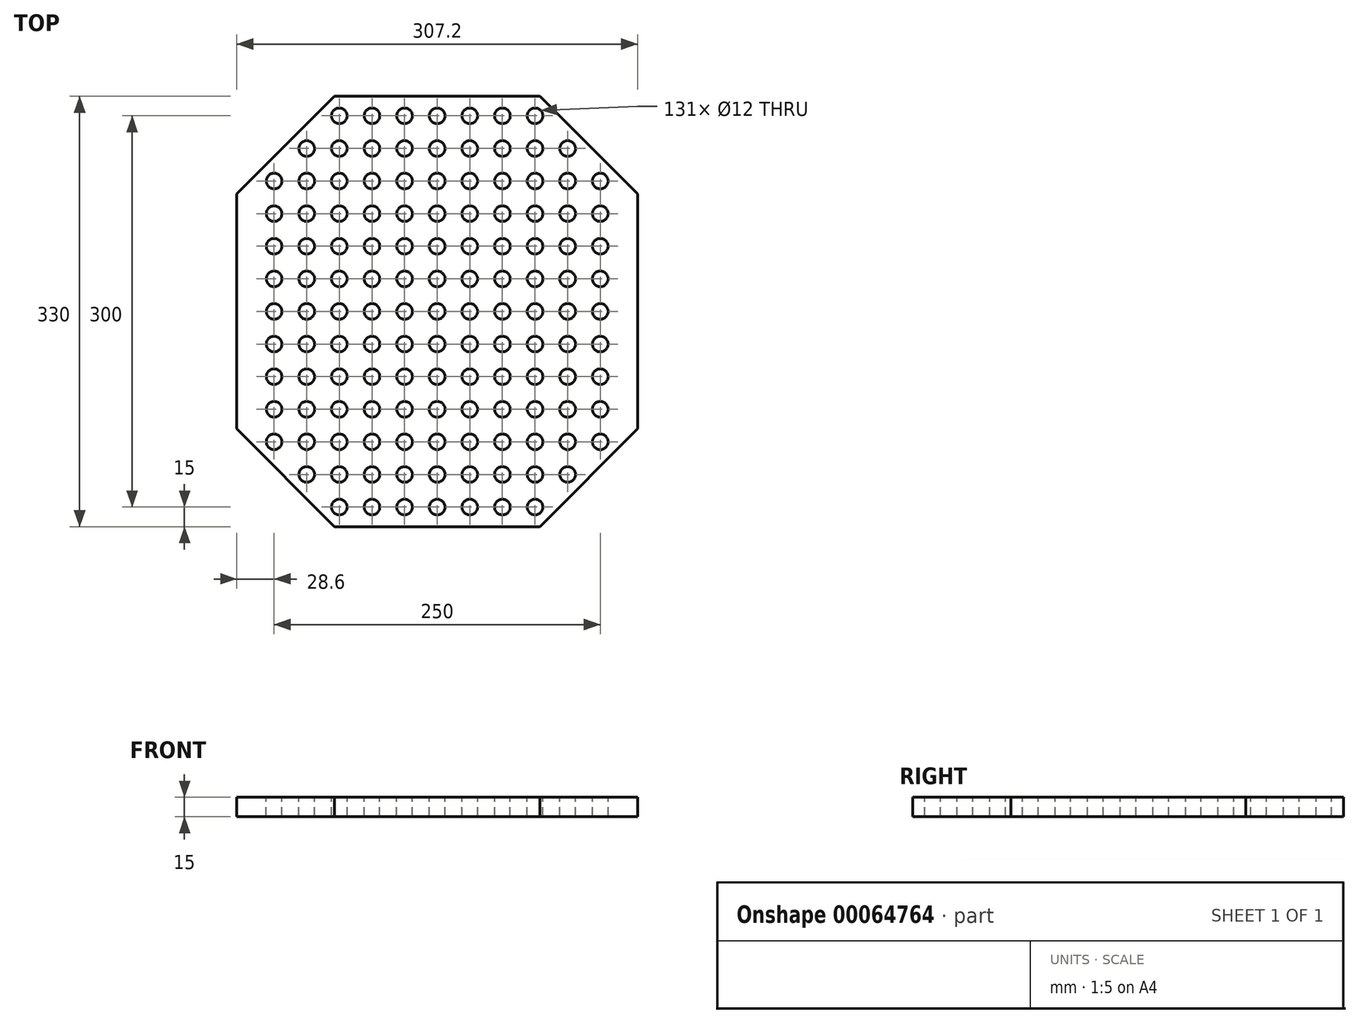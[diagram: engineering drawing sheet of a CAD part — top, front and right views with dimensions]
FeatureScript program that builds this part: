
annotation { "Feature Type Name" : "Feature", "Feature Type Description" : "" }
export const myFeature = defineFeature(function(context is Context, id is Id, definition is map)
    precondition{}
    {
        {
            var Q0;
            Q0=qCreatedBy(makeId("Top.planeOp"),FACE);
            var sketch = newSketch(context, id + "F0", { "sketchPlane" : qUnion([Q0])});
            skCircle(sketch, "E0", {"center": v(0, 0) * mm, "radius": 228.6 * mm, "construction": true});
            skLineSegment(sketch, "E1", {"start": v(0, 165) * mm, "end": v(78.6, 165) * mm});
            skLineSegment(sketch, "E2", {"start": v(78.6, 165) * mm, "end": v(153.6, 90) * mm});
            skLineSegment(sketch, "E3", {"start": v(153.6, 90) * mm, "end": v(153.6, 0) * mm});
            skLineSegment(sketch, "E4", {"start": v(0, 0) * mm, "end": v(0, 165) * mm, "construction": true});
            skLineSegment(sketch, "E5", {"start": v(0, 0) * mm, "end": v(153.6, 0) * mm, "construction": true});
            skLineSegment(sketch, "E6", {"start": v(0, 165) * mm, "end": v(0, 0) * mm});
            skLineSegment(sketch, "E7", {"start": v(0, 0) * mm, "end": v(153.6, 0) * mm});
            skSolve(sketch);
        }
        {
            var Q0;
            Q0 = qSketchRegion(id + "F0", true);
            extrude(context, id + "F1", {"entities" : qUnion([Q0]), "oppositeDirection" : true, "depth" : 15 * mm});
        }
        {
            var Q0;
            Q0=qCreatedBy(makeId("Top.planeOp"),FACE);
            var sketch = newSketch(context, id + "F2", { "sketchPlane" : qUnion([Q0])});
            skCircle(sketch, "E8", {"center": v(0, 0) * mm, "radius": 6 * mm});
            skCircle(sketch, "E9.0.1.0", {"center": v(0, 25) * mm, "radius": 6 * mm});
            skCircle(sketch, "E9.0.2.0", {"center": v(0, 50) * mm, "radius": 6 * mm});
            skCircle(sketch, "E9.0.3.0", {"center": v(0, 75) * mm, "radius": 6 * mm});
            skCircle(sketch, "E9.0.4.0", {"center": v(0, 100) * mm, "radius": 6 * mm});
            skCircle(sketch, "E9.0.5.0", {"center": v(0, 125) * mm, "radius": 6 * mm});
            skCircle(sketch, "E9.0.6.0", {"center": v(0, 150) * mm, "radius": 6 * mm});
            skCircle(sketch, "E9.1.0.0", {"center": v(25, 0) * mm, "radius": 6 * mm});
            skCircle(sketch, "E9.1.1.0", {"center": v(25, 25) * mm, "radius": 6 * mm});
            skCircle(sketch, "E9.1.2.0", {"center": v(25, 50) * mm, "radius": 6 * mm});
            skCircle(sketch, "E9.1.3.0", {"center": v(25, 75) * mm, "radius": 6 * mm});
            skCircle(sketch, "E9.1.4.0", {"center": v(25, 100) * mm, "radius": 6 * mm});
            skCircle(sketch, "E9.1.5.0", {"center": v(25, 125) * mm, "radius": 6 * mm});
            skCircle(sketch, "E9.1.6.0", {"center": v(25, 150) * mm, "radius": 6 * mm});
            skCircle(sketch, "E9.2.0.0", {"center": v(50, 0) * mm, "radius": 6 * mm});
            skCircle(sketch, "E9.2.1.0", {"center": v(50, 25) * mm, "radius": 6 * mm});
            skCircle(sketch, "E9.2.2.0", {"center": v(50, 50) * mm, "radius": 6 * mm});
            skCircle(sketch, "E9.2.3.0", {"center": v(50, 75) * mm, "radius": 6 * mm});
            skCircle(sketch, "E9.2.4.0", {"center": v(50, 100) * mm, "radius": 6 * mm});
            skCircle(sketch, "E9.2.5.0", {"center": v(50, 125) * mm, "radius": 6 * mm});
            skCircle(sketch, "E9.2.6.0", {"center": v(50, 150) * mm, "radius": 6 * mm});
            skCircle(sketch, "E9.3.0.0", {"center": v(75, 0) * mm, "radius": 6 * mm});
            skCircle(sketch, "E9.3.1.0", {"center": v(75, 25) * mm, "radius": 6 * mm});
            skCircle(sketch, "E9.3.2.0", {"center": v(75, 50) * mm, "radius": 6 * mm});
            skCircle(sketch, "E9.3.3.0", {"center": v(75, 75) * mm, "radius": 6 * mm});
            skCircle(sketch, "E9.3.4.0", {"center": v(75, 100) * mm, "radius": 6 * mm});
            skCircle(sketch, "E9.3.5.0", {"center": v(75, 125) * mm, "radius": 6 * mm});
            skCircle(sketch, "E9.3.6.0", {"center": v(75, 150) * mm, "radius": 6 * mm});
            skCircle(sketch, "E9.4.0.0", {"center": v(100, 0) * mm, "radius": 6 * mm});
            skCircle(sketch, "E9.4.1.0", {"center": v(100, 25) * mm, "radius": 6 * mm});
            skCircle(sketch, "E9.4.2.0", {"center": v(100, 50) * mm, "radius": 6 * mm});
            skCircle(sketch, "E9.4.3.0", {"center": v(100, 75) * mm, "radius": 6 * mm});
            skCircle(sketch, "E9.4.4.0", {"center": v(100, 100) * mm, "radius": 6 * mm});
            skCircle(sketch, "E9.4.5.0", {"center": v(100, 125) * mm, "radius": 6 * mm});
            skCircle(sketch, "E9.5.0.0", {"center": v(125, 0) * mm, "radius": 6 * mm});
            skCircle(sketch, "E9.5.1.0", {"center": v(125, 25) * mm, "radius": 6 * mm});
            skCircle(sketch, "E9.5.2.0", {"center": v(125, 50) * mm, "radius": 6 * mm});
            skCircle(sketch, "E9.5.3.0", {"center": v(125, 75) * mm, "radius": 6 * mm});
            skCircle(sketch, "E9.5.4.0", {"center": v(125, 100) * mm, "radius": 6 * mm});
            skLineSegment(sketch, "E9.direction1", {"start": v(0, 0) * mm, "end": v(25, 0) * mm, "construction": true});
            skLineSegment(sketch, "E9.direction2", {"start": v(0, 0) * mm, "end": v(0, 25) * mm, "construction": true});
            skSolve(sketch);
        }
        {
            var Q0;
            Q0 = qSketchRegion(id + "F2", true);
            extrude(context, id + "F3", {"entities" : qUnion([Q0]), "operationType" : NewBodyOperationType.REMOVE, "oppositeDirection" : true, "depth" : 25 * mm});
        }
        {
            var Q0;
            Q0=makeQuery(id+"F1.opExtrude","SWEPT_BODY",BODY,{"disambiguationData":[OSD([sQuery(id+"F0.wireOp",EDGE,"E1"),sQuery(id+"F0.wireOp",EDGE,"E2"),sQuery(id+"F0.wireOp",EDGE,"E3"),sQuery(id+"F0.wireOp",EDGE,"E6"),sQuery(id+"F0.wireOp",EDGE,"E7")])]});
            var Q1;
            Q1=qCreatedBy(makeId("Right.planeOp"),FACE);
            mirror(context, id + "F4", {"operationType" : NewBodyOperationType.ADD, "entities" : qUnion([Q0]), "mirrorPlane" : qUnion([Q1])});
        }
        {
            var Q0;
            Q0=makeQuery(id+"F1.opExtrude","SWEPT_BODY",BODY,{"disambiguationData":[OSD([sQuery(id+"F0.wireOp",EDGE,"E1"),sQuery(id+"F0.wireOp",EDGE,"E2"),sQuery(id+"F0.wireOp",EDGE,"E3"),sQuery(id+"F0.wireOp",EDGE,"E6"),sQuery(id+"F0.wireOp",EDGE,"E7")])]});
            var Q1;
            Q1=qCreatedBy(makeId("Front.planeOp"),FACE);
            mirror(context, id + "F5", {"operationType" : NewBodyOperationType.ADD, "entities" : qUnion([Q0]), "mirrorPlane" : qUnion([Q1])});
        }
    });
